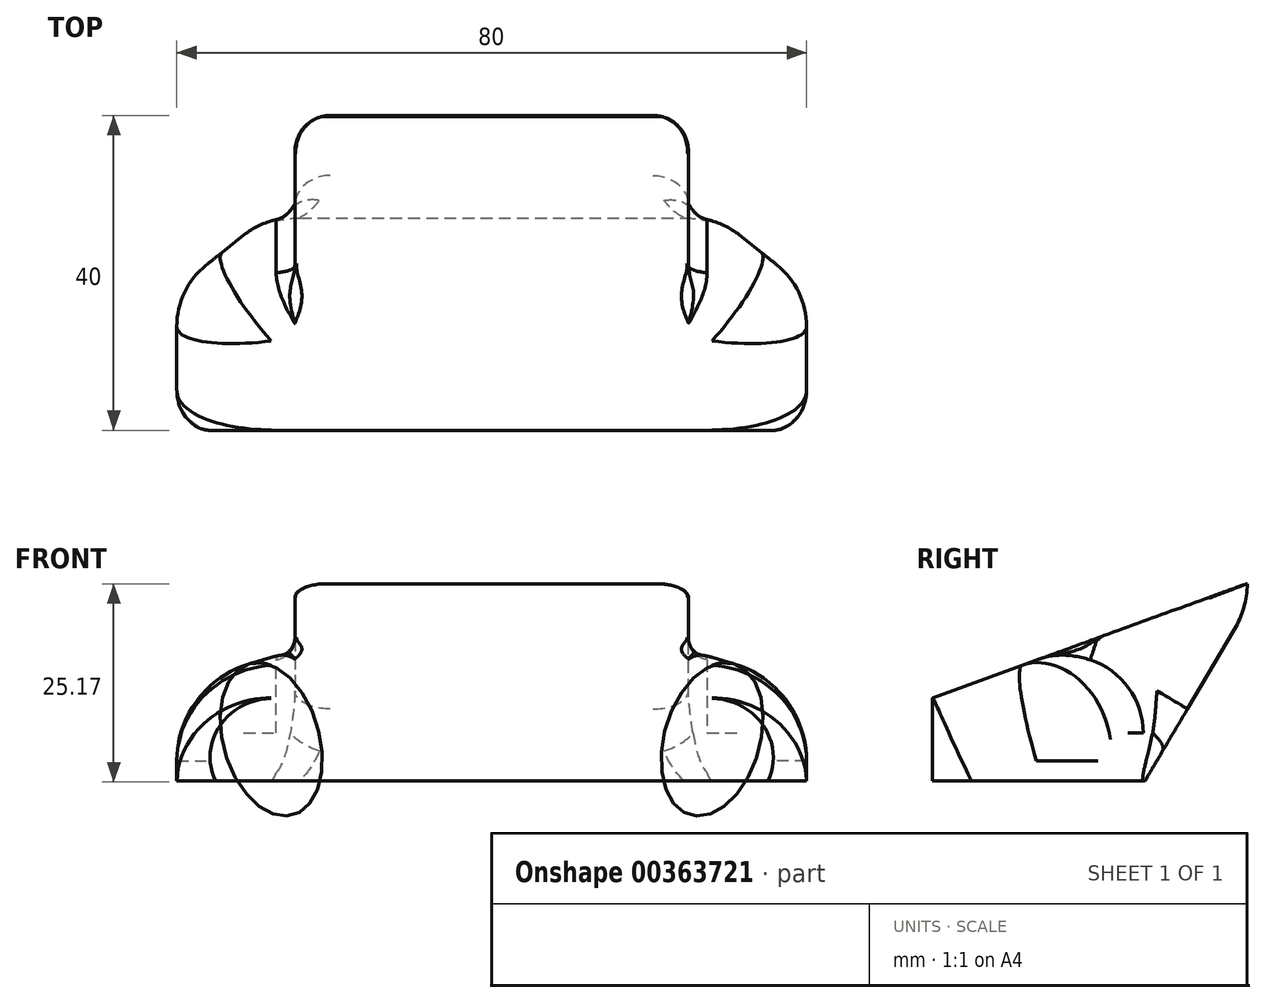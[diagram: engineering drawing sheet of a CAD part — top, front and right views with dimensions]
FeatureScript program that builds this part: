
annotation { "Feature Type Name" : "Feature", "Feature Type Description" : "" }
export const myFeature = defineFeature(function(context is Context, id is Id, definition is map)
    precondition{}
    {
        {
            var Q0;
            Q0=qCreatedBy(makeId("Top.planeOp"),FACE);
            var sketch = newSketch(context, id + "F0", { "sketchPlane" : qUnion([Q0])});
            skLineSegment(sketch, "E0", {"start": v(40, 0) * mm, "end": v(-40, 0) * mm});
            skLineSegment(sketch, "E1", {"start": v(-40, 0) * mm, "end": v(-40, 18) * mm});
            skLineSegment(sketch, "E2", {"start": v(-40, 18) * mm, "end": v(-28.75, 27) * mm});
            skLineSegment(sketch, "E3", {"start": v(-28.75, 27) * mm, "end": v(28.75, 27) * mm});
            skLineSegment(sketch, "E4", {"start": v(28.75, 27) * mm, "end": v(40, 18) * mm});
            skLineSegment(sketch, "E5", {"start": v(0, 40) * mm, "end": v(0, 0) * mm, "construction": true});
            skLineSegment(sketch, "E6", {"start": v(40, 18) * mm, "end": v(40, 0) * mm});
            skLineSegment(sketch, "E7", {"start": v(-25, 27) * mm, "end": v(-25, 40) * mm});
            skLineSegment(sketch, "E8", {"start": v(-25, 40) * mm, "end": v(25, 40) * mm});
            skLineSegment(sketch, "E9", {"start": v(25, 40) * mm, "end": v(25, 27) * mm});
            skSolve(sketch);
        }
        {
            var Q0;
            Q0 = qSketchRegion(id + "F0", true);
            extrude(context, id + "F1", {"entities" : qUnion([Q0]), "depth" : 25 * mm, "offsetDistance" : 25 * mm});
        }
        {
            var Q0;
            Q0=makeQuery(id+"F1.opExtrude","CAP_EDGE",EDGE,{"disambiguationData":[OSD([sQuery(id+"F0.wireOp",EDGE,"E0")])],"isStart":false});
            chamfer(context, id + "F2", {"entities" : qUnion([Q0]), "chamferType" : ChamferType.OFFSET_ANGLE, "width" : 14.5 * mm, "oppositeDirection" : false, "angle" : 70 * degree, "tangentPropagation" : true});
        }
        {
            var Q0;
            Q0=makeQuery(id+"F1.opExtrude","CAP_EDGE",EDGE,{"disambiguationData":[OSD([sQuery(id+"F0.wireOp",EDGE,"E8")])],"isStart":true});
            chamfer(context, id + "F3", {"entities" : qUnion([Q0]), "chamferType" : ChamferType.TWO_OFFSETS, "width1" : 13 * mm, "oppositeDirection" : false, "width2" : 22 * mm, "tangentPropagation" : true});
        }
        {
            var Q0;
            Q0=makeQuery(id+"F2.opChamfer","BLEND_EDGE",EDGE,{"blendedFrom":[makeQuery(id+"F1.opExtrude","CAP_EDGE",EDGE,{"disambiguationData":[OSD([sQuery(id+"F0.wireOp",EDGE,"E0")])],"isStart":false}),makeQuery(id+"F1.opExtrude","SWEPT_FACE",FACE,{"disambiguationData":[OSD([sQuery(id+"F0.wireOp",EDGE,"E1")])]})],"blendedInto":[makeQuery(id+"F1.opExtrude","SWEPT_FACE",FACE,{"disambiguationData":[OSD([sQuery(id+"F0.wireOp",EDGE,"E1")])]})]});
            var Q1;
            Q1=makeQuery(id+"F2.opChamfer","BLEND_EDGE",EDGE,{"blendedFrom":[makeQuery(id+"F1.opExtrude","CAP_EDGE",EDGE,{"disambiguationData":[OSD([sQuery(id+"F0.wireOp",EDGE,"E0")])],"isStart":false}),makeQuery(id+"F1.opExtrude","SWEPT_FACE",FACE,{"disambiguationData":[OSD([sQuery(id+"F0.wireOp",EDGE,"E6")])]})],"blendedInto":[makeQuery(id+"F1.opExtrude","SWEPT_FACE",FACE,{"disambiguationData":[OSD([sQuery(id+"F0.wireOp",EDGE,"E6")])]})]});
            var Q2;
            {var subQ0=sQuery(id+"F0.wireOp",EDGE,"E8");Q2=makeQuery(id+"F3.opChamfer","BLEND_EDGE",EDGE,{"blendedFrom":[makeQuery(id+"F1.opExtrude","CAP_EDGE",EDGE,{"disambiguationData":[OSD([subQ0])],"isStart":true}),makeQuery(id+"F1.opExtrude","SWEPT_FACE",FACE,{"disambiguationData":[OSD([subQ0])]})],"blendedInto":[makeQuery(id+"F1.opExtrude","SWEPT_FACE",FACE,{"disambiguationData":[OSD([subQ0])]})]});}
            fillet(context, id + "F4", {"entities" : qUnion([Q0, Q1, Q2]), "tangentPropagation" : true, "radius" : 12 * mm, "defaultsChanged" : false, "vertexSettings" : [], "allowEdgeOverflow" : false});
        }
        {
            var Q0;
            Q0=makeQuery(id+"F1.opExtrude","SWEPT_EDGE",EDGE,{"disambiguationData":[OSD([sQuery(id+"F0.wireOp",EDGE,"E2"),sQuery(id+"F0.wireOp",EDGE,"E3")])]});
            var Q1;
            Q1=makeQuery(id+"F1.opExtrude","SWEPT_EDGE",EDGE,{"disambiguationData":[OSD([sQuery(id+"F0.wireOp",EDGE,"E3"),sQuery(id+"F0.wireOp",EDGE,"E4")])]});
            fillet(context, id + "F5", {"entities" : qUnion([Q0, Q1]), "tangentPropagation" : true, "radius" : 10 * mm, "defaultsChanged" : true, "vertexSettings" : [], "allowEdgeOverflow" : false});
        }
        {
            var Q0;
            Q0=makeQuery(id+"F4.opFillet","BLEND_EDGE",EDGE,{"blendedFrom":[makeQuery(id+"F2.opChamfer","BLEND_EDGE",EDGE,{"blendedFrom":[makeQuery(id+"F1.opExtrude","CAP_EDGE",EDGE,{"disambiguationData":[OSD([sQuery(id+"F0.wireOp",EDGE,"E0")])],"isStart":false}),makeQuery(id+"F1.opExtrude","SWEPT_FACE",FACE,{"disambiguationData":[OSD([sQuery(id+"F0.wireOp",EDGE,"E6")])]})],"blendedInto":[makeQuery(id+"F1.opExtrude","SWEPT_FACE",FACE,{"disambiguationData":[OSD([sQuery(id+"F0.wireOp",EDGE,"E6")])]})]}),makeQuery(id+"F1.opExtrude","SWEPT_FACE",FACE,{"disambiguationData":[OSD([sQuery(id+"F0.wireOp",EDGE,"E4")])]})],"blendedInto":[makeQuery(id+"F1.opExtrude","SWEPT_FACE",FACE,{"disambiguationData":[OSD([sQuery(id+"F0.wireOp",EDGE,"E4")])]})]});
            var Q1;
            Q1=makeQuery(id+"F4.opFillet","BLEND_EDGE",EDGE,{"blendedFrom":[makeQuery(id+"F2.opChamfer","BLEND_EDGE",EDGE,{"blendedFrom":[makeQuery(id+"F1.opExtrude","CAP_EDGE",EDGE,{"disambiguationData":[OSD([sQuery(id+"F0.wireOp",EDGE,"E0")])],"isStart":false}),makeQuery(id+"F1.opExtrude","SWEPT_FACE",FACE,{"disambiguationData":[OSD([sQuery(id+"F0.wireOp",EDGE,"E1")])]})],"blendedInto":[makeQuery(id+"F1.opExtrude","SWEPT_FACE",FACE,{"disambiguationData":[OSD([sQuery(id+"F0.wireOp",EDGE,"E1")])]})]}),makeQuery(id+"F1.opExtrude","SWEPT_FACE",FACE,{"disambiguationData":[OSD([sQuery(id+"F0.wireOp",EDGE,"E2")])]})],"blendedInto":[makeQuery(id+"F1.opExtrude","SWEPT_FACE",FACE,{"disambiguationData":[OSD([sQuery(id+"F0.wireOp",EDGE,"E2")])]})]});
            fillet(context, id + "F6", {"entities" : qUnion([Q0, Q1]), "tangentPropagation" : true, "radius" : 10 * mm, "defaultsChanged" : true, "vertexSettings" : [], "allowEdgeOverflow" : false});
        }
        {
            var Q0;
            Q0=makeQuery(id+"F1.opExtrude","SWEPT_EDGE",EDGE,{"disambiguationData":[OSD([sQuery(id+"F0.wireOp",EDGE,"E3"),sQuery(id+"F0.wireOp",EDGE,"E9")])]});
            var Q1;
            Q1=makeQuery(id+"F1.opExtrude","SWEPT_EDGE",EDGE,{"disambiguationData":[OSD([sQuery(id+"F0.wireOp",EDGE,"E3"),sQuery(id+"F0.wireOp",EDGE,"E7")])]});
            fillet(context, id + "F7", {"entities" : qUnion([Q0, Q1]), "tangentPropagation" : true, "radius" : 3 * mm, "defaultsChanged" : true, "vertexSettings" : [], "allowEdgeOverflow" : false});
        }
        {
            var Q0;
            Q0=makeQuery(id+"F3.opChamfer","BLEND_EDGE",EDGE,{"blendedFrom":[makeQuery(id+"F1.opExtrude","CAP_EDGE",EDGE,{"disambiguationData":[OSD([sQuery(id+"F0.wireOp",EDGE,"E8")])],"isStart":true}),makeQuery(id+"F1.opExtrude","SWEPT_FACE",FACE,{"disambiguationData":[OSD([sQuery(id+"F0.wireOp",EDGE,"E7")])]})],"blendedInto":[makeQuery(id+"F1.opExtrude","SWEPT_FACE",FACE,{"disambiguationData":[OSD([sQuery(id+"F0.wireOp",EDGE,"E7")])]})]});
            var Q1;
            Q1=makeQuery(id+"F1.opExtrude","SWEPT_EDGE",EDGE,{"disambiguationData":[OSD([sQuery(id+"F0.wireOp",EDGE,"E7"),sQuery(id+"F0.wireOp",EDGE,"E8")])]});
            var Q2;
            Q2=makeQuery(id+"F1.opExtrude","SWEPT_EDGE",EDGE,{"disambiguationData":[OSD([sQuery(id+"F0.wireOp",EDGE,"E8"),sQuery(id+"F0.wireOp",EDGE,"E9")])]});
            var Q3;
            Q3=makeQuery(id+"F3.opChamfer","BLEND_EDGE",EDGE,{"blendedFrom":[makeQuery(id+"F1.opExtrude","CAP_EDGE",EDGE,{"disambiguationData":[OSD([sQuery(id+"F0.wireOp",EDGE,"E8")])],"isStart":true}),makeQuery(id+"F1.opExtrude","SWEPT_FACE",FACE,{"disambiguationData":[OSD([sQuery(id+"F0.wireOp",EDGE,"E9")])]})],"blendedInto":[makeQuery(id+"F1.opExtrude","SWEPT_FACE",FACE,{"disambiguationData":[OSD([sQuery(id+"F0.wireOp",EDGE,"E9")])]})]});
            fillet(context, id + "F8", {"entities" : qUnion([Q0, Q1, Q2, Q3]), "tangentPropagation" : true, "radius" : 4.5 * mm, "defaultsChanged" : true, "vertexSettings" : [], "allowEdgeOverflow" : false});
        }
        {
            var Q0;
            {var subQ0=sQuery(id+"F0.wireOp",EDGE,"E0");var subQ1=sQuery(id+"F0.wireOp",EDGE,"E9");var subQ2=sQuery(id+"F0.wireOp",EDGE,"E3");Q0=makeQuery(id+"F7.opFillet","BLEND_EDGE",EDGE,{"blendedFrom":[makeQuery(id+"F6.opFillet","BLEND_EDGE",EDGE,{"blendedFrom":[makeQuery(id+"F2.opChamfer","BLEND_EDGE",EDGE,{"blendedFrom":[makeQuery(id+"F1.opExtrude","CAP_EDGE",EDGE,{"disambiguationData":[OSD([subQ0])],"isStart":false}),makeQuery(id+"F1.opExtrude","SWEPT_FACE",FACE,{"disambiguationData":[OSD([subQ2]),TDD([makeQuery(id+"F0.imprint","IMPRINT",EDGE,{"disambiguationData":[TD([[makeQuery(id+"F0.imprint","INTERSECT",VERTEX,{"derivedFrom":[subQ2,sQuery(id+"F0.wireOp",EDGE,"E4")]}),1.0]])],"derivedFrom":subQ2})])]})],"blendedInto":[makeQuery(id+"F1.opExtrude","SWEPT_FACE",FACE,{"disambiguationData":[OSD([subQ2]),TDD([makeQuery(id+"F0.imprint","IMPRINT",EDGE,{"disambiguationData":[TD([[makeQuery(id+"F0.imprint","INTERSECT",VERTEX,{"derivedFrom":[subQ2,sQuery(id+"F0.wireOp",EDGE,"E4")]}),1.0]])],"derivedFrom":subQ2})])]})]}),makeQuery(id+"F1.opExtrude","SWEPT_FACE",FACE,{"disambiguationData":[OSD([subQ1])]})],"blendedInto":[makeQuery(id+"F1.opExtrude","SWEPT_FACE",FACE,{"disambiguationData":[OSD([subQ1])]})]}),makeQuery(id+"F2.opChamfer","BLEND_FACE",FACE,{"disambiguationData":[OSD([subQ0])]})],"blendedInto":[makeQuery(id+"F2.opChamfer","BLEND_FACE",FACE,{"disambiguationData":[OSD([subQ0])]})]});}
            var Q1;
            {var subQ0=sQuery(id+"F0.wireOp",EDGE,"E0");var subQ1=sQuery(id+"F0.wireOp",EDGE,"E7");var subQ2=sQuery(id+"F0.wireOp",EDGE,"E3");Q1=makeQuery(id+"F7.opFillet","BLEND_EDGE",EDGE,{"blendedFrom":[makeQuery(id+"F6.opFillet","BLEND_EDGE",EDGE,{"blendedFrom":[makeQuery(id+"F2.opChamfer","BLEND_EDGE",EDGE,{"blendedFrom":[makeQuery(id+"F1.opExtrude","CAP_EDGE",EDGE,{"disambiguationData":[OSD([subQ0])],"isStart":false}),makeQuery(id+"F1.opExtrude","SWEPT_FACE",FACE,{"disambiguationData":[OSD([subQ2]),TDD([makeQuery(id+"F0.imprint","IMPRINT",EDGE,{"disambiguationData":[TD([[makeQuery(id+"F0.imprint","INTERSECT",VERTEX,{"derivedFrom":[sQuery(id+"F0.wireOp",EDGE,"E2"),subQ2]}),-1.0]])],"derivedFrom":subQ2})])]})],"blendedInto":[makeQuery(id+"F1.opExtrude","SWEPT_FACE",FACE,{"disambiguationData":[OSD([subQ2]),TDD([makeQuery(id+"F0.imprint","IMPRINT",EDGE,{"disambiguationData":[TD([[makeQuery(id+"F0.imprint","INTERSECT",VERTEX,{"derivedFrom":[sQuery(id+"F0.wireOp",EDGE,"E2"),subQ2]}),-1.0]])],"derivedFrom":subQ2})])]})]}),makeQuery(id+"F1.opExtrude","SWEPT_FACE",FACE,{"disambiguationData":[OSD([subQ1])]})],"blendedInto":[makeQuery(id+"F1.opExtrude","SWEPT_FACE",FACE,{"disambiguationData":[OSD([subQ1])]})]}),makeQuery(id+"F2.opChamfer","BLEND_FACE",FACE,{"disambiguationData":[OSD([subQ0])]})],"blendedInto":[makeQuery(id+"F2.opChamfer","BLEND_FACE",FACE,{"disambiguationData":[OSD([subQ0])]})]});}
            var Q2;
            {var subQ0=sQuery(id+"F0.wireOp",EDGE,"E0");var subQ1=sQuery(id+"F0.wireOp",EDGE,"E8");var subQ2=sQuery(id+"F0.wireOp",EDGE,"E7");Q2=makeQuery(id+"F8.opFillet","BLEND_VERTEX",VERTEX,{"blendedFrom":[makeQuery(id+"F4.opFillet","BLEND_EDGE",EDGE,{"blendedFrom":[makeQuery(id+"F3.opChamfer","BLEND_EDGE",EDGE,{"blendedFrom":[makeQuery(id+"F1.opExtrude","CAP_EDGE",EDGE,{"disambiguationData":[OSD([subQ1])],"isStart":true}),makeQuery(id+"F1.opExtrude","SWEPT_FACE",FACE,{"disambiguationData":[OSD([subQ1])]})],"blendedInto":[makeQuery(id+"F1.opExtrude","SWEPT_FACE",FACE,{"disambiguationData":[OSD([subQ1])]})]}),makeQuery(id+"F1.opExtrude","SWEPT_FACE",FACE,{"disambiguationData":[OSD([subQ2])]})],"blendedInto":[makeQuery(id+"F1.opExtrude","SWEPT_FACE",FACE,{"disambiguationData":[OSD([subQ2])]})]}),makeQuery(id+"F1.opExtrude","CAP_FACE",FACE,{"disambiguationData":[OSD([subQ0,sQuery(id+"F0.wireOp",EDGE,"E1"),sQuery(id+"F0.wireOp",EDGE,"E2"),sQuery(id+"F0.wireOp",EDGE,"E3"),sQuery(id+"F0.wireOp",EDGE,"E4"),sQuery(id+"F0.wireOp",EDGE,"E6"),subQ2,subQ1,sQuery(id+"F0.wireOp",EDGE,"E9")])],"isStart":false}),makeQuery(id+"F2.opChamfer","BLEND_FACE",FACE,{"disambiguationData":[OSD([subQ0])]})],"blendedInto":[makeQuery(id+"F1.opExtrude","CAP_FACE",FACE,{"disambiguationData":[OSD([subQ0,sQuery(id+"F0.wireOp",EDGE,"E1"),sQuery(id+"F0.wireOp",EDGE,"E2"),sQuery(id+"F0.wireOp",EDGE,"E3"),sQuery(id+"F0.wireOp",EDGE,"E4"),sQuery(id+"F0.wireOp",EDGE,"E6"),subQ2,subQ1,sQuery(id+"F0.wireOp",EDGE,"E9")])],"isStart":false}),makeQuery(id+"F2.opChamfer","BLEND_FACE",FACE,{"disambiguationData":[OSD([subQ0])]})]});}
            var Q3;
            {var subQ0=sQuery(id+"F0.wireOp",EDGE,"E0");var subQ1=sQuery(id+"F0.wireOp",EDGE,"E9");var subQ2=sQuery(id+"F0.wireOp",EDGE,"E8");Q3=makeQuery(id+"F8.opFillet","BLEND_VERTEX",VERTEX,{"blendedFrom":[makeQuery(id+"F4.opFillet","BLEND_EDGE",EDGE,{"blendedFrom":[makeQuery(id+"F3.opChamfer","BLEND_EDGE",EDGE,{"blendedFrom":[makeQuery(id+"F1.opExtrude","CAP_EDGE",EDGE,{"disambiguationData":[OSD([subQ2])],"isStart":true}),makeQuery(id+"F1.opExtrude","SWEPT_FACE",FACE,{"disambiguationData":[OSD([subQ2])]})],"blendedInto":[makeQuery(id+"F1.opExtrude","SWEPT_FACE",FACE,{"disambiguationData":[OSD([subQ2])]})]}),makeQuery(id+"F1.opExtrude","SWEPT_FACE",FACE,{"disambiguationData":[OSD([subQ1])]})],"blendedInto":[makeQuery(id+"F1.opExtrude","SWEPT_FACE",FACE,{"disambiguationData":[OSD([subQ1])]})]}),makeQuery(id+"F1.opExtrude","CAP_FACE",FACE,{"disambiguationData":[OSD([subQ0,sQuery(id+"F0.wireOp",EDGE,"E1"),sQuery(id+"F0.wireOp",EDGE,"E2"),sQuery(id+"F0.wireOp",EDGE,"E3"),sQuery(id+"F0.wireOp",EDGE,"E4"),sQuery(id+"F0.wireOp",EDGE,"E6"),sQuery(id+"F0.wireOp",EDGE,"E7"),subQ2,subQ1])],"isStart":false}),makeQuery(id+"F2.opChamfer","BLEND_FACE",FACE,{"disambiguationData":[OSD([subQ0])]})],"blendedInto":[makeQuery(id+"F1.opExtrude","CAP_FACE",FACE,{"disambiguationData":[OSD([subQ0,sQuery(id+"F0.wireOp",EDGE,"E1"),sQuery(id+"F0.wireOp",EDGE,"E2"),sQuery(id+"F0.wireOp",EDGE,"E3"),sQuery(id+"F0.wireOp",EDGE,"E4"),sQuery(id+"F0.wireOp",EDGE,"E6"),sQuery(id+"F0.wireOp",EDGE,"E7"),subQ2,subQ1])],"isStart":false}),makeQuery(id+"F2.opChamfer","BLEND_FACE",FACE,{"disambiguationData":[OSD([subQ0])]})]});}
            var Q4;
            {var subQ0=makeQuery(id+"F1.opExtrude","SWEPT_FACE",FACE,{"disambiguationData":[OSD([sQuery(id+"F0.wireOp",EDGE,"E7")])]});var subQ1=sQuery(id+"F0.wireOp",EDGE,"E8");Q4=makeQuery(id+"F8.opFillet","BLEND_VERTEX",VERTEX,{"blendedFrom":[makeQuery(id+"F4.opFillet","BLEND_EDGE",EDGE,{"blendedFrom":[makeQuery(id+"F3.opChamfer","BLEND_EDGE",EDGE,{"blendedFrom":[makeQuery(id+"F1.opExtrude","CAP_EDGE",EDGE,{"disambiguationData":[OSD([subQ1])],"isStart":true}),makeQuery(id+"F1.opExtrude","SWEPT_FACE",FACE,{"disambiguationData":[OSD([subQ1])]})],"blendedInto":[makeQuery(id+"F1.opExtrude","SWEPT_FACE",FACE,{"disambiguationData":[OSD([subQ1])]})]}),subQ0],"blendedInto":[subQ0]}),subQ0,makeQuery(id+"F2.opChamfer","BLEND_FACE",FACE,{"disambiguationData":[OSD([sQuery(id+"F0.wireOp",EDGE,"E0")])]})],"blendedInto":[subQ0,makeQuery(id+"F2.opChamfer","BLEND_FACE",FACE,{"disambiguationData":[OSD([sQuery(id+"F0.wireOp",EDGE,"E0")])]})]});}
            var Q5;
            {var subQ0=makeQuery(id+"F1.opExtrude","SWEPT_FACE",FACE,{"disambiguationData":[OSD([sQuery(id+"F0.wireOp",EDGE,"E9")])]});var subQ1=sQuery(id+"F0.wireOp",EDGE,"E8");Q5=makeQuery(id+"F8.opFillet","BLEND_VERTEX",VERTEX,{"blendedFrom":[makeQuery(id+"F4.opFillet","BLEND_EDGE",EDGE,{"blendedFrom":[makeQuery(id+"F3.opChamfer","BLEND_EDGE",EDGE,{"blendedFrom":[makeQuery(id+"F1.opExtrude","CAP_EDGE",EDGE,{"disambiguationData":[OSD([subQ1])],"isStart":true}),makeQuery(id+"F1.opExtrude","SWEPT_FACE",FACE,{"disambiguationData":[OSD([subQ1])]})],"blendedInto":[makeQuery(id+"F1.opExtrude","SWEPT_FACE",FACE,{"disambiguationData":[OSD([subQ1])]})]}),subQ0],"blendedInto":[subQ0]}),subQ0,makeQuery(id+"F2.opChamfer","BLEND_FACE",FACE,{"disambiguationData":[OSD([sQuery(id+"F0.wireOp",EDGE,"E0")])]})],"blendedInto":[subQ0,makeQuery(id+"F2.opChamfer","BLEND_FACE",FACE,{"disambiguationData":[OSD([sQuery(id+"F0.wireOp",EDGE,"E0")])]})]});}
            var Q6;
            {var subQ0=sQuery(id+"F0.wireOp",EDGE,"E0");var subQ1=sQuery(id+"F0.wireOp",EDGE,"E9");var subQ2=makeQuery(id+"F1.opExtrude","SWEPT_FACE",FACE,{"disambiguationData":[OSD([subQ1])]});var subQ3=sQuery(id+"F0.wireOp",EDGE,"E3");Q6=makeQuery(id+"F7.opFillet","BLEND_VERTEX",VERTEX,{"blendedFrom":[makeQuery(id+"F6.opFillet","BLEND_EDGE",EDGE,{"blendedFrom":[makeQuery(id+"F2.opChamfer","BLEND_EDGE",EDGE,{"blendedFrom":[makeQuery(id+"F1.opExtrude","CAP_EDGE",EDGE,{"disambiguationData":[OSD([subQ0])],"isStart":false}),makeQuery(id+"F1.opExtrude","SWEPT_FACE",FACE,{"disambiguationData":[OSD([subQ3]),TDD([makeQuery(id+"F0.imprint","IMPRINT",EDGE,{"disambiguationData":[TD([[makeQuery(id+"F0.imprint","INTERSECT",VERTEX,{"derivedFrom":[subQ3,sQuery(id+"F0.wireOp",EDGE,"E4")]}),1.0]])],"derivedFrom":subQ3})])]})],"blendedInto":[makeQuery(id+"F1.opExtrude","SWEPT_FACE",FACE,{"disambiguationData":[OSD([subQ3]),TDD([makeQuery(id+"F0.imprint","IMPRINT",EDGE,{"disambiguationData":[TD([[makeQuery(id+"F0.imprint","INTERSECT",VERTEX,{"derivedFrom":[subQ3,sQuery(id+"F0.wireOp",EDGE,"E4")]}),1.0]])],"derivedFrom":subQ3})])]})]}),subQ2],"blendedInto":[subQ2]}),subQ2,makeQuery(id+"F2.opChamfer","BLEND_FACE",FACE,{"disambiguationData":[OSD([subQ0])]})],"blendedInto":[subQ2,makeQuery(id+"F2.opChamfer","BLEND_FACE",FACE,{"disambiguationData":[OSD([subQ0])]})]});}
            var Q7;
            {var subQ0=sQuery(id+"F0.wireOp",EDGE,"E0");var subQ1=sQuery(id+"F0.wireOp",EDGE,"E7");var subQ2=makeQuery(id+"F1.opExtrude","SWEPT_FACE",FACE,{"disambiguationData":[OSD([subQ1])]});var subQ3=sQuery(id+"F0.wireOp",EDGE,"E3");Q7=makeQuery(id+"F7.opFillet","BLEND_VERTEX",VERTEX,{"blendedFrom":[makeQuery(id+"F6.opFillet","BLEND_EDGE",EDGE,{"blendedFrom":[makeQuery(id+"F2.opChamfer","BLEND_EDGE",EDGE,{"blendedFrom":[makeQuery(id+"F1.opExtrude","CAP_EDGE",EDGE,{"disambiguationData":[OSD([subQ0])],"isStart":false}),makeQuery(id+"F1.opExtrude","SWEPT_FACE",FACE,{"disambiguationData":[OSD([subQ3]),TDD([makeQuery(id+"F0.imprint","IMPRINT",EDGE,{"disambiguationData":[TD([[makeQuery(id+"F0.imprint","INTERSECT",VERTEX,{"derivedFrom":[sQuery(id+"F0.wireOp",EDGE,"E2"),subQ3]}),-1.0]])],"derivedFrom":subQ3})])]})],"blendedInto":[makeQuery(id+"F1.opExtrude","SWEPT_FACE",FACE,{"disambiguationData":[OSD([subQ3]),TDD([makeQuery(id+"F0.imprint","IMPRINT",EDGE,{"disambiguationData":[TD([[makeQuery(id+"F0.imprint","INTERSECT",VERTEX,{"derivedFrom":[sQuery(id+"F0.wireOp",EDGE,"E2"),subQ3]}),-1.0]])],"derivedFrom":subQ3})])]})]}),subQ2],"blendedInto":[subQ2]}),subQ2,makeQuery(id+"F2.opChamfer","BLEND_FACE",FACE,{"disambiguationData":[OSD([subQ0])]})],"blendedInto":[subQ2,makeQuery(id+"F2.opChamfer","BLEND_FACE",FACE,{"disambiguationData":[OSD([subQ0])]})]});}
            fillet(context, id + "F9", {"entities" : qUnion([Q0, Q1]), "tangentPropagation" : true, "radius" : 5 * mm, "defaultsChanged" : false, "isVariable" : true, "vertexSettings" : [{ "vertex" : qUnion([Q2]), "vertexRadius" : { 'value' : try(0 * mm), 'expression' : "0 mm" }.value, "variableRho" : { 'value' : try(0.5), 'expression' : "0.5" }.value, "variableMagnitude" : { 'value' : try(0.5), 'expression' : "0.5" }.value }, { "vertex" : qUnion([Q3]), "vertexRadius" : { 'value' : try(0 * mm), 'expression' : "0 mm" }.value, "variableRho" : { 'value' : try(0.5), 'expression' : "0.5" }.value, "variableMagnitude" : { 'value' : try(0.5), 'expression' : "0.5" }.value }, { "vertex" : qUnion([Q4]), "vertexRadius" : { 'value' : try(0.1 * mm), 'expression' : "0.1 mm" }.value, "variableRho" : { 'value' : try(0.5), 'expression' : "0.5" }.value, "variableMagnitude" : { 'value' : try(0.5), 'expression' : "0.5" }.value }, { "vertex" : qUnion([Q5]), "vertexRadius" : { 'value' : try(0.1 * mm), 'expression' : "0.1 mm" }.value, "variableRho" : { 'value' : try(0.5), 'expression' : "0.5" }.value, "variableMagnitude" : { 'value' : try(0.5), 'expression' : "0.5" }.value }, { "vertex" : qUnion([Q6]), "vertexRadius" : { 'value' : try(0.2 * mm), 'expression' : "0.2 mm" }.value, "variableRho" : { 'value' : try(0.5), 'expression' : "0.5" }.value, "variableMagnitude" : { 'value' : try(0.5), 'expression' : "0.5" }.value }, { "vertex" : qUnion([Q7]), "vertexRadius" : { 'value' : try(0.2 * mm), 'expression' : "0.2 mm" }.value, "variableRho" : { 'value' : try(0.5), 'expression' : "0.5" }.value, "variableMagnitude" : { 'value' : try(0.5), 'expression' : "0.5" }.value }], "smoothTransition" : false, "allowEdgeOverflow" : false});
        }
        {
            var Q0;
            {var subQ0=sQuery(id+"F0.wireOp",EDGE,"E0");Q0=makeQuery(id+"F4.opFillet","BLEND_EDGE",EDGE,{"blendedFrom":[makeQuery(id+"F2.opChamfer","BLEND_EDGE",EDGE,{"blendedFrom":[makeQuery(id+"F1.opExtrude","CAP_EDGE",EDGE,{"disambiguationData":[OSD([subQ0])],"isStart":false}),makeQuery(id+"F1.opExtrude","SWEPT_FACE",FACE,{"disambiguationData":[OSD([sQuery(id+"F0.wireOp",EDGE,"E6")])]})],"blendedInto":[makeQuery(id+"F1.opExtrude","SWEPT_FACE",FACE,{"disambiguationData":[OSD([sQuery(id+"F0.wireOp",EDGE,"E6")])]})]}),makeQuery(id+"F1.opExtrude","SWEPT_FACE",FACE,{"disambiguationData":[OSD([subQ0])]})],"blendedInto":[makeQuery(id+"F1.opExtrude","SWEPT_FACE",FACE,{"disambiguationData":[OSD([subQ0])]})]});}
            var Q1;
            {var subQ0=sQuery(id+"F0.wireOp",EDGE,"E0");Q1=makeQuery(id+"F4.opFillet","BLEND_EDGE",EDGE,{"blendedFrom":[makeQuery(id+"F2.opChamfer","BLEND_EDGE",EDGE,{"blendedFrom":[makeQuery(id+"F1.opExtrude","CAP_EDGE",EDGE,{"disambiguationData":[OSD([subQ0])],"isStart":false}),makeQuery(id+"F1.opExtrude","SWEPT_FACE",FACE,{"disambiguationData":[OSD([sQuery(id+"F0.wireOp",EDGE,"E1")])]})],"blendedInto":[makeQuery(id+"F1.opExtrude","SWEPT_FACE",FACE,{"disambiguationData":[OSD([sQuery(id+"F0.wireOp",EDGE,"E1")])]})]}),makeQuery(id+"F1.opExtrude","SWEPT_FACE",FACE,{"disambiguationData":[OSD([subQ0])]})],"blendedInto":[makeQuery(id+"F1.opExtrude","SWEPT_FACE",FACE,{"disambiguationData":[OSD([subQ0])]})]});}
            var Q2;
            {var subQ0=sQuery(id+"F0.wireOp",EDGE,"E0");Q2=makeQuery(id+"F4.opFillet","BLEND_VERTEX",VERTEX,{"blendedFrom":[makeQuery(id+"F2.opChamfer","BLEND_EDGE",EDGE,{"blendedFrom":[makeQuery(id+"F1.opExtrude","CAP_EDGE",EDGE,{"disambiguationData":[OSD([subQ0])],"isStart":false}),makeQuery(id+"F1.opExtrude","SWEPT_FACE",FACE,{"disambiguationData":[OSD([sQuery(id+"F0.wireOp",EDGE,"E1")])]})],"blendedInto":[makeQuery(id+"F1.opExtrude","SWEPT_FACE",FACE,{"disambiguationData":[OSD([sQuery(id+"F0.wireOp",EDGE,"E1")])]})]}),makeQuery(id+"F2.opChamfer","BLEND_FACE",FACE,{"disambiguationData":[OSD([subQ0])]}),makeQuery(id+"F1.opExtrude","SWEPT_FACE",FACE,{"disambiguationData":[OSD([subQ0])]})],"blendedInto":[makeQuery(id+"F2.opChamfer","BLEND_FACE",FACE,{"disambiguationData":[OSD([subQ0])]}),makeQuery(id+"F1.opExtrude","SWEPT_FACE",FACE,{"disambiguationData":[OSD([subQ0])]})]});}
            var Q3;
            {var subQ0=sQuery(id+"F0.wireOp",EDGE,"E1");var subQ1=sQuery(id+"F0.wireOp",EDGE,"E0");Q3=makeQuery(id+"F4.opFillet","BLEND_VERTEX",VERTEX,{"blendedFrom":[makeQuery(id+"F2.opChamfer","BLEND_EDGE",EDGE,{"blendedFrom":[makeQuery(id+"F1.opExtrude","CAP_EDGE",EDGE,{"disambiguationData":[OSD([subQ1])],"isStart":false}),makeQuery(id+"F1.opExtrude","SWEPT_FACE",FACE,{"disambiguationData":[OSD([subQ0])]})],"blendedInto":[makeQuery(id+"F1.opExtrude","SWEPT_FACE",FACE,{"disambiguationData":[OSD([subQ0])]})]}),makeQuery(id+"F1.opExtrude","SWEPT_FACE",FACE,{"disambiguationData":[OSD([subQ1])]}),makeQuery(id+"F1.opExtrude","CAP_FACE",FACE,{"disambiguationData":[OSD([subQ1,subQ0,sQuery(id+"F0.wireOp",EDGE,"E2"),sQuery(id+"F0.wireOp",EDGE,"E3"),sQuery(id+"F0.wireOp",EDGE,"E4"),sQuery(id+"F0.wireOp",EDGE,"E6"),sQuery(id+"F0.wireOp",EDGE,"E7"),sQuery(id+"F0.wireOp",EDGE,"E8"),sQuery(id+"F0.wireOp",EDGE,"E9")])],"isStart":true})],"blendedInto":[makeQuery(id+"F1.opExtrude","SWEPT_FACE",FACE,{"disambiguationData":[OSD([subQ1])]}),makeQuery(id+"F1.opExtrude","CAP_FACE",FACE,{"disambiguationData":[OSD([subQ1,subQ0,sQuery(id+"F0.wireOp",EDGE,"E2"),sQuery(id+"F0.wireOp",EDGE,"E3"),sQuery(id+"F0.wireOp",EDGE,"E4"),sQuery(id+"F0.wireOp",EDGE,"E6"),sQuery(id+"F0.wireOp",EDGE,"E7"),sQuery(id+"F0.wireOp",EDGE,"E8"),sQuery(id+"F0.wireOp",EDGE,"E9")])],"isStart":true})]});}
            var Q4;
            {var subQ0=sQuery(id+"F0.wireOp",EDGE,"E0");Q4=makeQuery(id+"F4.opFillet","BLEND_VERTEX",VERTEX,{"blendedFrom":[makeQuery(id+"F2.opChamfer","BLEND_EDGE",EDGE,{"blendedFrom":[makeQuery(id+"F1.opExtrude","CAP_EDGE",EDGE,{"disambiguationData":[OSD([subQ0])],"isStart":false}),makeQuery(id+"F1.opExtrude","SWEPT_FACE",FACE,{"disambiguationData":[OSD([sQuery(id+"F0.wireOp",EDGE,"E6")])]})],"blendedInto":[makeQuery(id+"F1.opExtrude","SWEPT_FACE",FACE,{"disambiguationData":[OSD([sQuery(id+"F0.wireOp",EDGE,"E6")])]})]}),makeQuery(id+"F2.opChamfer","BLEND_FACE",FACE,{"disambiguationData":[OSD([subQ0])]}),makeQuery(id+"F1.opExtrude","SWEPT_FACE",FACE,{"disambiguationData":[OSD([subQ0])]})],"blendedInto":[makeQuery(id+"F2.opChamfer","BLEND_FACE",FACE,{"disambiguationData":[OSD([subQ0])]}),makeQuery(id+"F1.opExtrude","SWEPT_FACE",FACE,{"disambiguationData":[OSD([subQ0])]})]});}
            fillet(context, id + "F10", {"entities" : qUnion([Q0, Q1]), "tangentPropagation" : true, "radius" : 5 * mm, "defaultsChanged" : false, "isVariable" : true, "vertexSettings" : [{ "vertex" : qUnion([Q2]), "vertexRadius" : { 'value' : try(0.1 * mm), 'expression' : "0.1 mm" }.value, "variableRho" : { 'value' : try(0.5), 'expression' : "0.5" }.value, "variableMagnitude" : { 'value' : try(0.5), 'expression' : "0.5" }.value }, { "vertex" : qUnion([Q3]), "vertexRadius" : { 'value' : try(5 * mm), 'expression' : "5 mm" }.value, "variableRho" : { 'value' : try(0.5), 'expression' : "0.5" }.value, "variableMagnitude" : { 'value' : try(0.5), 'expression' : "0.5" }.value }, { "vertex" : qUnion([Q4]), "vertexRadius" : { 'value' : try(0.1 * mm), 'expression' : "0.1 mm" }.value, "variableRho" : { 'value' : try(0.5), 'expression' : "0.5" }.value, "variableMagnitude" : { 'value' : try(0.5), 'expression' : "0.5" }.value }], "smoothTransition" : false, "allowEdgeOverflow" : false});
        }
    });
